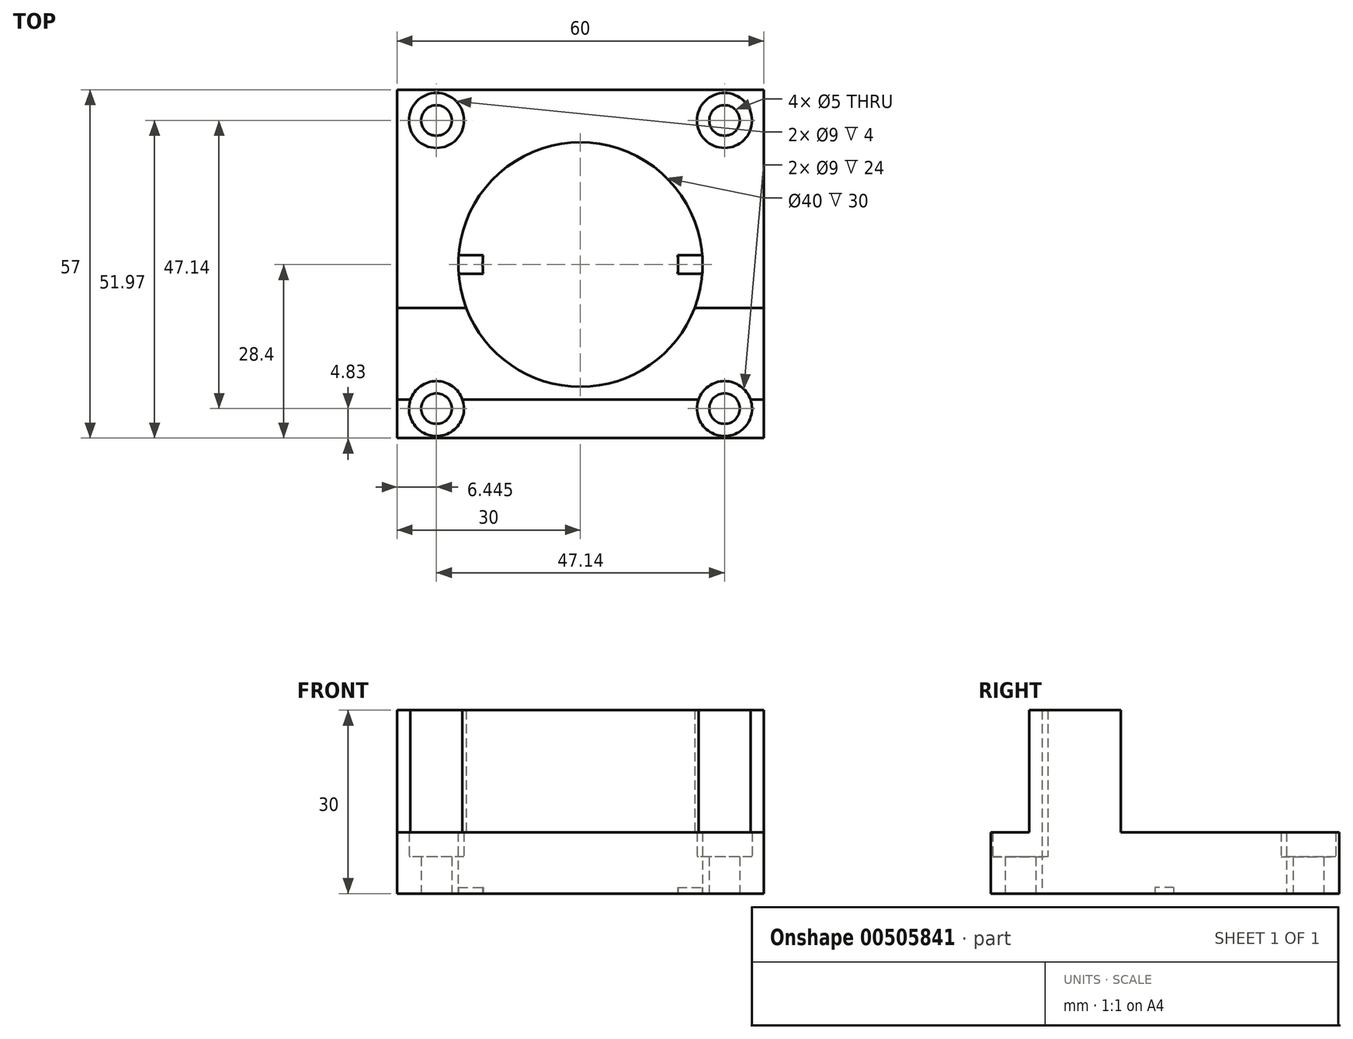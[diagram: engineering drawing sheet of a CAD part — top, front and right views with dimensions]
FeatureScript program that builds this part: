
annotation { "Feature Type Name" : "Feature", "Feature Type Description" : "" }
export const myFeature = defineFeature(function(context is Context, id is Id, definition is map)
    precondition{}
    {
        {
            var Q0;
            Q0=qCreatedBy(makeId("Top.planeOp"),FACE);
            var sketch = newSketch(context, id + "F0", { "sketchPlane" : qUnion([Q0])});
            skLineSegment(sketch, "E0.bottom", {"start": v(0, 0) * mm, "end": v(60, 0) * mm});
            skLineSegment(sketch, "E0.top", {"start": v(0, 57) * mm, "end": v(60, 57) * mm});
            skLineSegment(sketch, "E0.left", {"start": v(0, 0) * mm, "end": v(0, 57) * mm});
            skLineSegment(sketch, "E0.right", {"start": v(60, 0) * mm, "end": v(60, 57) * mm});
            skLineSegment(sketch, "E1", {"start": v(0, 6.3) * mm, "end": v(2.2, 6.3) * mm});
            skCircle(sketch, "E2", {"center": v(30, 28.4) * mm, "radius": 20 * mm});
            skLineSegment(sketch, "E3", {"start": v(0, 21.3) * mm, "end": v(11.3, 21.3) * mm});
            skCircle(sketch, "E4", {"center": v(6.44, 51.97) * mm, "radius": 2.5 * mm});
            skCircle(sketch, "E5", {"center": v(6.44, 4.83) * mm, "radius": 2.5 * mm});
            skCircle(sketch, "E6", {"center": v(53.58, 51.97) * mm, "radius": 2.5 * mm});
            skCircle(sketch, "E7", {"center": v(53.58, 4.83) * mm, "radius": 2.5 * mm});
            skCircle(sketch, "E8", {"center": v(6.44, 4.83) * mm, "radius": 4.5 * mm});
            skCircle(sketch, "E9", {"center": v(53.58, 4.83) * mm, "radius": 4.5 * mm});
            skLineSegment(sketch, "E10.trimOffspring", {"start": v(48.7, 21.3) * mm, "end": v(60, 21.3) * mm});
            skLineSegment(sketch, "E11.trimOffspring", {"start": v(10.7, 6.3) * mm, "end": v(49.33, 6.3) * mm});
            skLineSegment(sketch, "E12.trimOffspring", {"start": v(57.84, 6.3) * mm, "end": v(60, 6.3) * mm});
            skCircle(sketch, "E13", {"center": v(6.44, 51.97) * mm, "radius": 4.5 * mm});
            skCircle(sketch, "E14", {"center": v(53.58, 51.97) * mm, "radius": 4.5 * mm});
            skCircle(sketch, "E15", {"center": v(30, 28.4) * mm, "radius": 16 * mm});
            skLineSegment(sketch, "E16", {"start": v(10.06, 29.93) * mm, "end": v(14.07, 29.93) * mm});
            skLineSegment(sketch, "E17", {"start": v(14.07, 26.87) * mm, "end": v(10.06, 26.87) * mm});
            skLineSegment(sketch, "E18", {"start": v(45.93, 29.93) * mm, "end": v(49.94, 29.93) * mm});
            skLineSegment(sketch, "E19", {"start": v(45.93, 26.87) * mm, "end": v(49.94, 26.87) * mm});
            skSolve(sketch);
        }
        {
            var Q0;
            {var subQ4=sQuery(id+"F0.wireOp",EDGE,"E0.top");Q0=makeQuery(id+"F0.imprint","IMPRINT",FACE,{"disambiguationData":[TD([[makeQuery(id+"F0.imprint","IMPRINT",EDGE,{"derivedFrom":subQ4}),-1.0]])]});}
            extrude(context, id + "F1", {"entities" : qUnion([Q0]), "depth" : 10 * mm});
        }
        {
            var Q0;
            {var subQ5=sQuery(id+"F0.wireOp",EDGE,"E1");Q0=makeQuery(id+"F0.imprint","IMPRINT",FACE,{"disambiguationData":[TD([[makeQuery(id+"F0.imprint","IMPRINT",EDGE,{"derivedFrom":subQ5}),1.0]])]});}
            extrude(context, id + "F2", {"entities" : qUnion([Q0]), "operationType" : NewBodyOperationType.ADD, "depth" : 30 * mm});
        }
        {
            var Q0;
            {var subQ5=sQuery(id+"F0.wireOp",EDGE,"E0.bottom");Q0=makeQuery(id+"F0.imprint","IMPRINT",FACE,{"disambiguationData":[TD([[makeQuery(id+"F0.imprint","IMPRINT",EDGE,{"derivedFrom":subQ5}),1.0]])]});}
            extrude(context, id + "F3", {"entities" : qUnion([Q0]), "operationType" : NewBodyOperationType.ADD, "depth" : 10 * mm});
        }
        {
            var Q0;
            Q0=makeQuery(id+"F0.imprint","IMPRINT",FACE,{"disambiguationData":[TD([[makeQuery(id+"F0.imprint","IMPRINT",EDGE,{"derivedFrom":sQuery(id+"F0.wireOp",EDGE,"E5")}),-1.0]])]});
            extrude(context, id + "F4", {"entities" : qUnion([Q0]), "operationType" : NewBodyOperationType.ADD, "depth" : 6 * mm});
        }
        {
            var Q0;
            Q0=makeQuery(id+"F0.imprint","IMPRINT",FACE,{"disambiguationData":[TD([[makeQuery(id+"F0.imprint","IMPRINT",EDGE,{"derivedFrom":sQuery(id+"F0.wireOp",EDGE,"E7")}),-1.0]])]});
            extrude(context, id + "F5", {"entities" : qUnion([Q0]), "operationType" : NewBodyOperationType.ADD, "depth" : 6 * mm});
        }
        {
            var Q0;
            Q0=makeQuery(id+"F0.imprint","IMPRINT",FACE,{"disambiguationData":[TD([[makeQuery(id+"F0.imprint","IMPRINT",EDGE,{"derivedFrom":sQuery(id+"F0.wireOp",EDGE,"E4")}),-1.0]])]});
            var Q1;
            Q1=makeQuery(id+"F0.imprint","IMPRINT",FACE,{"disambiguationData":[TD([[makeQuery(id+"F0.imprint","IMPRINT",EDGE,{"derivedFrom":sQuery(id+"F0.wireOp",EDGE,"E6")}),-1.0]])]});
            extrude(context, id + "F6", {"entities" : qUnion([Q0, Q1]), "operationType" : NewBodyOperationType.ADD, "depth" : 6 * mm});
        }
        {
            var Q0;
            {var subQ0=sQuery(id+"F0.wireOp",EDGE,"E16");Q0=makeQuery(id+"F0.imprint","IMPRINT",FACE,{"disambiguationData":[TD([[makeQuery(id+"F0.imprint","IMPRINT",EDGE,{"derivedFrom":subQ0}),-1.0]])]});}
            var Q1;
            {var subQ0=sQuery(id+"F0.wireOp",EDGE,"E18");Q1=makeQuery(id+"F0.imprint","IMPRINT",FACE,{"disambiguationData":[TD([[makeQuery(id+"F0.imprint","IMPRINT",EDGE,{"derivedFrom":subQ0}),-1.0]])]});}
            extrude(context, id + "F7", {"entities" : qUnion([Q0, Q1]), "depth" : 1 * mm});
        }
    });
